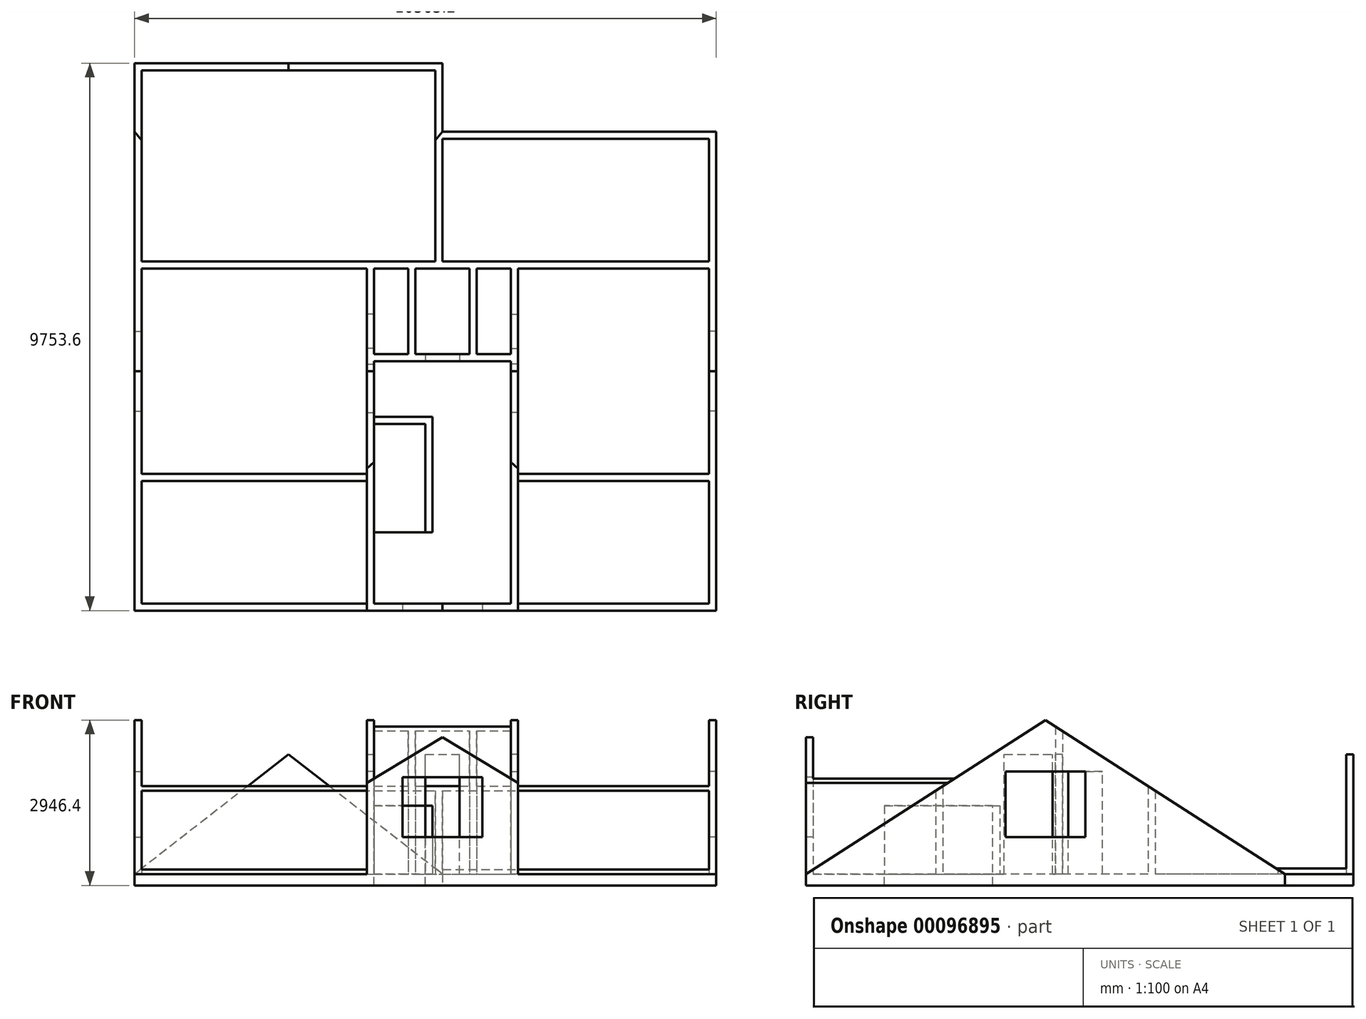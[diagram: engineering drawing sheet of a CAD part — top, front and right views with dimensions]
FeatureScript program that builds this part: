
annotation { "Feature Type Name" : "Feature", "Feature Type Description" : "" }
export const myFeature = defineFeature(function(context is Context, id is Id, definition is map)
    precondition{}
    {
        {
            var Q0;
            Q0=qCreatedBy(makeId("Top.planeOp"),FACE);
            var sketch = newSketch(context, id + "F0", { "sketchPlane" : qUnion([Q0])});
            skLineSegment(sketch, "E0", {"start": v(0, 0) * mm, "end": v(10363.2, 0) * mm});
            skLineSegment(sketch, "E1", {"start": v(10363.2, 0) * mm, "end": v(10363.2, 8534.4) * mm});
            skLineSegment(sketch, "E2", {"start": v(10363.2, 8534.4) * mm, "end": v(5486.4, 8534.4) * mm});
            skLineSegment(sketch, "E3", {"start": v(0, 9753.6) * mm, "end": v(0, 0) * mm});
            skLineSegment(sketch, "E4.bottom", {"start": v(127, 2311.4) * mm, "end": v(4140.2, 2311.4) * mm});
            skLineSegment(sketch, "E4.top", {"start": v(127, 127) * mm, "end": v(4140.2, 127) * mm});
            skLineSegment(sketch, "E4.left", {"start": v(127, 2311.4) * mm, "end": v(127, 127) * mm});
            skLineSegment(sketch, "E4.right", {"start": v(4140.2, 2311.4) * mm, "end": v(4140.2, 127) * mm});
            skLineSegment(sketch, "E5.bottom", {"start": v(4267.2, 127) * mm, "end": v(6705.6, 127) * mm});
            skLineSegment(sketch, "E5.top", {"start": v(4267.2, 4445) * mm, "end": v(6705.6, 4445) * mm});
            skLineSegment(sketch, "E5.left", {"start": v(4267.2, 127) * mm, "end": v(4267.2, 4445) * mm});
            skLineSegment(sketch, "E5.right", {"start": v(6705.6, 127) * mm, "end": v(6705.6, 4445) * mm});
            skLineSegment(sketch, "E6.bottom", {"start": v(6832.6, 2311.4) * mm, "end": v(10236.2, 2311.4) * mm});
            skLineSegment(sketch, "E6.top", {"start": v(6832.6, 127) * mm, "end": v(10236.2, 127) * mm});
            skLineSegment(sketch, "E6.left", {"start": v(6832.6, 2311.4) * mm, "end": v(6832.6, 127) * mm});
            skLineSegment(sketch, "E6.right", {"start": v(10236.2, 2311.4) * mm, "end": v(10236.2, 127) * mm});
            skLineSegment(sketch, "E7.left", {"start": v(127, 9626.6) * mm, "end": v(127, 6223) * mm});
            skLineSegment(sketch, "E8.bottom", {"start": v(5486.4, 8407.4) * mm, "end": v(10236.2, 8407.4) * mm});
            skLineSegment(sketch, "E8.right", {"start": v(10236.2, 8407.4) * mm, "end": v(10236.2, 6223) * mm});
            skLineSegment(sketch, "E9.bottom", {"start": v(4267.2, 6096) * mm, "end": v(4876.8, 6096) * mm});
            skLineSegment(sketch, "E9.top", {"start": v(4267.2, 4572) * mm, "end": v(4876.8, 4572) * mm});
            skLineSegment(sketch, "E9.left", {"start": v(4267.2, 6096) * mm, "end": v(4267.2, 4572) * mm});
            skLineSegment(sketch, "E9.right", {"start": v(4876.8, 6096) * mm, "end": v(4876.8, 4572) * mm});
            skLineSegment(sketch, "E10.bottom", {"start": v(5003.8, 6096) * mm, "end": v(5969, 6096) * mm});
            skLineSegment(sketch, "E10.top", {"start": v(5003.8, 4572) * mm, "end": v(5969, 4572) * mm});
            skLineSegment(sketch, "E10.left", {"start": v(5003.8, 6096) * mm, "end": v(5003.8, 4572) * mm});
            skLineSegment(sketch, "E10.right", {"start": v(5969, 6096) * mm, "end": v(5969, 4572) * mm});
            skLineSegment(sketch, "E11.bottom", {"start": v(6096, 6096) * mm, "end": v(6705.6, 6096) * mm});
            skLineSegment(sketch, "E11.top", {"start": v(6096, 4572) * mm, "end": v(6705.6, 4572) * mm});
            skLineSegment(sketch, "E11.left", {"start": v(6096, 6096) * mm, "end": v(6096, 4572) * mm});
            skLineSegment(sketch, "E11.right", {"start": v(6705.6, 6096) * mm, "end": v(6705.6, 4572) * mm});
            skLineSegment(sketch, "E12.bottom", {"start": v(127, 6096) * mm, "end": v(4140.2, 6096) * mm});
            skLineSegment(sketch, "E12.top", {"start": v(127, 2438.4) * mm, "end": v(4140.2, 2438.4) * mm});
            skLineSegment(sketch, "E12.left", {"start": v(127, 6096) * mm, "end": v(127, 2438.4) * mm});
            skLineSegment(sketch, "E12.right", {"start": v(4140.2, 6096) * mm, "end": v(4140.2, 2438.4) * mm});
            skLineSegment(sketch, "E13.bottom", {"start": v(6832.6, 6096) * mm, "end": v(10236.2, 6096) * mm});
            skLineSegment(sketch, "E13.top", {"start": v(6832.6, 2438.4) * mm, "end": v(10236.2, 2438.4) * mm});
            skLineSegment(sketch, "E13.left", {"start": v(6832.6, 6096) * mm, "end": v(6832.6, 2438.4) * mm});
            skLineSegment(sketch, "E13.right", {"start": v(10236.2, 6096) * mm, "end": v(10236.2, 2438.4) * mm});
            skLineSegment(sketch, "E14", {"start": v(0, 9753.6) * mm, "end": v(5486.4, 9753.6) * mm});
            skLineSegment(sketch, "E15", {"start": v(127, 6223) * mm, "end": v(5359.4, 6223) * mm});
            skLineSegment(sketch, "E16", {"start": v(5486.4, 9753.6) * mm, "end": v(5486.4, 8534.4) * mm});
            skLineSegment(sketch, "E17", {"start": v(127, 9626.6) * mm, "end": v(5359.4, 9626.6) * mm});
            skLineSegment(sketch, "E18", {"start": v(5359.4, 9626.6) * mm, "end": v(5359.4, 6223) * mm});
            skLineSegment(sketch, "E19.trimOffspring", {"start": v(5486.4, 8407.4) * mm, "end": v(5486.4, 6223) * mm});
            skLineSegment(sketch, "E20.trimOffspring", {"start": v(5486.4, 6223) * mm, "end": v(10236.2, 6223) * mm});
            skSolve(sketch);
        }
        {
            var Q0;
            Q0 = qSketchRegion(id + "F0", true);
            extrude(context, id + "F1", {"entities" : qUnion([Q0]), "depth" : 2743.2 * mm});
        }
        {
            var Q0;
            Q0=qCreatedBy(makeId("Top.planeOp"),FACE);
            var sketch = newSketch(context, id + "F2", { "sketchPlane" : qUnion([Q0])});
            skLineSegment(sketch, "E21.bottom", {"start": v(4267.2, 3327.4) * mm, "end": v(5181.6, 3327.4) * mm});
            skLineSegment(sketch, "E21.top", {"start": v(4267.2, 1397) * mm, "end": v(5181.6, 1397) * mm});
            skLineSegment(sketch, "E21.left", {"start": v(4267.2, 3327.4) * mm, "end": v(4267.2, 1397) * mm});
            skLineSegment(sketch, "E21.right", {"start": v(5181.6, 3327.4) * mm, "end": v(5181.6, 1397) * mm});
            skLineSegment(sketch, "E22", {"start": v(0, 0) * mm, "end": v(0, 9753.6) * mm});
            skLineSegment(sketch, "E23", {"start": v(0, 9753.6) * mm, "end": v(5486.4, 9753.6) * mm});
            skLineSegment(sketch, "E24", {"start": v(5486.4, 9753.6) * mm, "end": v(5486.4, 8534.4) * mm});
            skLineSegment(sketch, "E25", {"start": v(5486.4, 8534.4) * mm, "end": v(10363.2, 8534.4) * mm});
            skLineSegment(sketch, "E26", {"start": v(10363.2, 8534.4) * mm, "end": v(10363.2, 0) * mm});
            skLineSegment(sketch, "E27", {"start": v(10363.2, 0) * mm, "end": v(0, 0) * mm});
            skSolve(sketch);
        }
        {
            var Q0;
            Q0 = qSketchRegion(id + "F2", true);
            extrude(context, id + "F3", {"entities" : qUnion([Q0]), "operationType" : NewBodyOperationType.ADD, "oppositeDirection" : true, "depth" : 203.2 * mm});
        }
        {
            var Q0;
            Q0=makeQuery(id+"F1.opExtrude","SWEPT_FACE",FACE,{"disambiguationData":[OSD([sQuery(id+"F0.wireOp",EDGE,"E5.right")])]});
            var sketch = newSketch(context, id + "F4", { "sketchPlane" : qUnion([Q0])});
            skLineSegment(sketch, "E28.bottom", {"start": v(-4394.2, 0) * mm, "end": v(-3530.6, 0) * mm});
            skLineSegment(sketch, "E28.top", {"start": v(-4394.2, 2133.6) * mm, "end": v(-3530.6, 2133.6) * mm});
            skLineSegment(sketch, "E28.left", {"start": v(-4394.2, 0) * mm, "end": v(-4394.2, 2133.6) * mm});
            skLineSegment(sketch, "E28.right", {"start": v(-3530.6, 0) * mm, "end": v(-3530.6, 2133.6) * mm});
            skSolve(sketch);
        }
        {
            var Q0;
            Q0 = qSketchRegion(id + "F4", true);
            extrude(context, id + "F5", {"entities" : qUnion([Q0]), "operationType" : NewBodyOperationType.REMOVE, "endBound" : BoundingType.UP_TO_NEXT, "oppositeDirection" : true, "depth" : 25.4 * mm});
        }
        {
            var Q0;
            Q0=makeQuery(id+"F3.boolean.opBoolean","MERGE",FACE,{"derivedFrom":[makeQuery(id+"F1.opExtrude","SWEPT_FACE",FACE,{"disambiguationData":[OSD([sQuery(id+"F0.wireOp",EDGE,"E5.left")])]}),makeQuery(id+"F3.opExtrude","SWEPT_FACE",FACE,{"disambiguationData":[OSD([sQuery(id+"F2.wireOp",EDGE,"E21.left")])]})]});
            var sketch = newSketch(context, id + "F6", { "sketchPlane" : qUnion([Q0])});
            skLineSegment(sketch, "E29.bottom", {"start": v(3530.6, 0) * mm, "end": v(4394.2, 0) * mm});
            skLineSegment(sketch, "E29.top", {"start": v(3530.6, 2133.6) * mm, "end": v(4394.2, 2133.6) * mm});
            skLineSegment(sketch, "E29.left", {"start": v(3530.6, 0) * mm, "end": v(3530.6, 2133.6) * mm});
            skLineSegment(sketch, "E29.right", {"start": v(4394.2, 0) * mm, "end": v(4394.2, 2133.6) * mm});
            skSolve(sketch);
        }
        {
            var Q0;
            Q0 = qSketchRegion(id + "F6", true);
            extrude(context, id + "F7", {"entities" : qUnion([Q0]), "operationType" : NewBodyOperationType.REMOVE, "endBound" : BoundingType.UP_TO_NEXT, "oppositeDirection" : true, "depth" : 25.4 * mm});
        }
        {
            var Q0;
            Q0=makeQuery(id+"F1.opExtrude","SWEPT_FACE",FACE,{"disambiguationData":[OSD([sQuery(id+"F0.wireOp",EDGE,"E5.top")])]});
            var sketch = newSketch(context, id + "F8", { "sketchPlane" : qUnion([Q0])});
            skLineSegment(sketch, "E30.bottom", {"start": v(5181.6, 0) * mm, "end": v(5791.2, 0) * mm});
            skLineSegment(sketch, "E30.top", {"start": v(5181.6, 2133.6) * mm, "end": v(5791.2, 2133.6) * mm});
            skLineSegment(sketch, "E30.left", {"start": v(5181.6, 0) * mm, "end": v(5181.6, 2133.6) * mm});
            skLineSegment(sketch, "E30.right", {"start": v(5791.2, 0) * mm, "end": v(5791.2, 2133.6) * mm});
            skSolve(sketch);
        }
        {
            var Q0;
            Q0 = qSketchRegion(id + "F8", true);
            extrude(context, id + "F9", {"entities" : qUnion([Q0]), "operationType" : NewBodyOperationType.REMOVE, "endBound" : BoundingType.UP_TO_NEXT, "oppositeDirection" : true, "depth" : 25.4 * mm});
        }
        {
            var Q0;
            Q0=makeQuery(id+"F1.opExtrude","SWEPT_FACE",FACE,{"disambiguationData":[OSD([sQuery(id+"F0.wireOp",EDGE,"E13.right")])]});
            var sketch = newSketch(context, id + "F10", { "sketchPlane" : qUnion([Q0])});
            skLineSegment(sketch, "E31.bottom", {"start": v(-4978.4, 1828.8) * mm, "end": v(-3556, 1828.8) * mm});
            skLineSegment(sketch, "E31.top", {"start": v(-4978.4, 660.4) * mm, "end": v(-3556, 660.4) * mm});
            skLineSegment(sketch, "E31.left", {"start": v(-4978.4, 1828.8) * mm, "end": v(-4978.4, 660.4) * mm});
            skLineSegment(sketch, "E31.right", {"start": v(-3556, 1828.8) * mm, "end": v(-3556, 660.4) * mm});
            skSolve(sketch);
        }
        {
            var Q0;
            Q0 = qSketchRegion(id + "F10", true);
            extrude(context, id + "F11", {"entities" : qUnion([Q0]), "operationType" : NewBodyOperationType.REMOVE, "endBound" : BoundingType.UP_TO_NEXT, "oppositeDirection" : true, "depth" : 25.4 * mm});
        }
        {
            var Q0;
            Q0=makeQuery(id+"F1.opExtrude","SWEPT_FACE",FACE,{"disambiguationData":[OSD([sQuery(id+"F0.wireOp",EDGE,"E13.left")])]});
            var sketch = newSketch(context, id + "F12", { "sketchPlane" : qUnion([Q0])});
            skLineSegment(sketch, "E32.bottom", {"start": v(4673.6, 0) * mm, "end": v(5283.2, 0) * mm});
            skLineSegment(sketch, "E32.top", {"start": v(4673.6, 1828.8) * mm, "end": v(5283.2, 1828.8) * mm});
            skLineSegment(sketch, "E32.left", {"start": v(4673.6, 0) * mm, "end": v(4673.6, 1828.8) * mm});
            skLineSegment(sketch, "E32.right", {"start": v(5283.2, 0) * mm, "end": v(5283.2, 1828.8) * mm});
            skSolve(sketch);
        }
        {
            var Q0;
            Q0 = qSketchRegion(id + "F12", true);
            extrude(context, id + "F13", {"entities" : qUnion([Q0]), "operationType" : NewBodyOperationType.REMOVE, "endBound" : BoundingType.UP_TO_NEXT, "oppositeDirection" : true, "depth" : 25.4 * mm});
        }
        {
            var Q0;
            Q0=makeQuery(id+"F1.opExtrude","SWEPT_FACE",FACE,{"disambiguationData":[OSD([sQuery(id+"F0.wireOp",EDGE,"E12.left")])]});
            var sketch = newSketch(context, id + "F14", { "sketchPlane" : qUnion([Q0])});
            skLineSegment(sketch, "E33.bottom", {"start": v(3556, 1828.8) * mm, "end": v(4978.4, 1828.8) * mm});
            skLineSegment(sketch, "E33.top", {"start": v(3556, 660.4) * mm, "end": v(4978.4, 660.4) * mm});
            skLineSegment(sketch, "E33.left", {"start": v(3556, 1828.8) * mm, "end": v(3556, 660.4) * mm});
            skLineSegment(sketch, "E33.right", {"start": v(4978.4, 1828.8) * mm, "end": v(4978.4, 660.4) * mm});
            skSolve(sketch);
        }
        {
            var Q0;
            Q0 = qSketchRegion(id + "F14", true);
            extrude(context, id + "F15", {"entities" : qUnion([Q0]), "operationType" : NewBodyOperationType.REMOVE, "endBound" : BoundingType.UP_TO_NEXT, "oppositeDirection" : true, "depth" : 25.4 * mm});
        }
        {
            var Q0;
            Q0=makeQuery(id+"F1.opExtrude","SWEPT_FACE",FACE,{"disambiguationData":[OSD([sQuery(id+"F0.wireOp",EDGE,"E12.right")])]});
            var sketch = newSketch(context, id + "F16", { "sketchPlane" : qUnion([Q0])});
            skLineSegment(sketch, "E34.bottom", {"start": v(-5283.2, 0) * mm, "end": v(-4673.6, 0) * mm});
            skLineSegment(sketch, "E34.top", {"start": v(-5283.2, 1828.8) * mm, "end": v(-4673.6, 1828.8) * mm});
            skLineSegment(sketch, "E34.left", {"start": v(-5283.2, 0) * mm, "end": v(-5283.2, 1828.8) * mm});
            skLineSegment(sketch, "E34.right", {"start": v(-4673.6, 0) * mm, "end": v(-4673.6, 1828.8) * mm});
            skSolve(sketch);
        }
        {
            var Q0;
            Q0 = qSketchRegion(id + "F16", true);
            extrude(context, id + "F17", {"entities" : qUnion([Q0]), "operationType" : NewBodyOperationType.REMOVE, "endBound" : BoundingType.UP_TO_NEXT, "oppositeDirection" : true, "depth" : 25.4 * mm});
        }
        {
            var Q0;
            Q0=makeQuery(id+"F3.boolean.opBoolean","MERGE",FACE,{"derivedFrom":[makeQuery(id+"F1.opExtrude","SWEPT_FACE",FACE,{"disambiguationData":[OSD([sQuery(id+"F0.wireOp",EDGE,"E1")])]}),makeQuery(id+"F3.opExtrude","SWEPT_FACE",FACE,{"disambiguationData":[OSD([sQuery(id+"F2.wireOp",EDGE,"O0DFnVWc-X87s-zQva-5IaV-f9uga9J4KueF")])]})]});
            var sketch = newSketch(context, id + "F18", { "sketchPlane" : qUnion([Q0])});
            skLineSegment(sketch, "E35", {"start": v(0, 0) * mm, "end": v(8534.4, 0) * mm, "construction": true});
            skLineSegment(sketch, "E36", {"start": v(4267.2, 0) * mm, "end": v(4267.2, 2743.2) * mm, "construction": true});
            skPoint(sketch, "E36.endSnap0", {"position": v(4267.2, 2743.2) * mm});
            skLineSegment(sketch, "E37", {"start": v(0, 0) * mm, "end": v(4267.2, 2743.2) * mm});
            skLineSegment(sketch, "E38", {"start": v(8534.4, 0) * mm, "end": v(4267.2, 2743.2) * mm});
            skLineSegment(sketch, "E39", {"start": v(0, 0) * mm, "end": v(0, 2743.2) * mm});
            skLineSegment(sketch, "E40", {"start": v(0, 2743.2) * mm, "end": v(8534.4, 2743.2) * mm});
            skLineSegment(sketch, "E41", {"start": v(8534.4, 2743.2) * mm, "end": v(8534.4, 0) * mm});
            skSolve(sketch);
        }
        {
            var Q0;
            Q0 = qSketchRegion(id + "F18", true);
            extrude(context, id + "F19", {"entities" : qUnion([Q0]), "operationType" : NewBodyOperationType.REMOVE, "endBound" : BoundingType.THROUGH_ALL, "oppositeDirection" : true, "depth" : 25.4 * mm});
        }
        {
            var Q0;
            {var subQ0=sQuery(id+"F2.wireOp",EDGE,"E21.bottom");var subQ1=sQuery(id+"F2.wireOp",EDGE,"E21.top");var subQ2=sQuery(id+"F2.wireOp",EDGE,"E21.left");var subQ3=sQuery(id+"F2.wireOp",EDGE,"E21.right");var subQ4=makeQuery(id+"F3.opExtrude","CAP_FACE",FACE,{"disambiguationData":[OSD([subQ0,subQ1,subQ2,subQ3,sQuery(id+"F2.wireOp",EDGE,"E22"),sQuery(id+"F2.wireOp",EDGE,"E23"),sQuery(id+"F2.wireOp",EDGE,"E24"),sQuery(id+"F2.wireOp",EDGE,"E25"),sQuery(id+"F2.wireOp",EDGE,"E26"),sQuery(id+"F2.wireOp",EDGE,"E27")])],"isStart":true});Q0=makeQuery(id+"F17.boolean.opBoolean","MERGE",FACE,{"derivedFrom":[makeQuery(id+"F3.boolean.opBoolean","SPLIT",FACE,{"disambiguationData":[TD([makeQuery(id+"F1.opExtrude","SWEPT_FACE",FACE,{"disambiguationData":[OSD([sQuery(id+"F0.wireOp",EDGE,"E9.bottom")])]})])],"derivedFrom":subQ4}),makeQuery(id+"F13.boolean.opBoolean","MERGE",FACE,{"derivedFrom":[makeQuery(id+"F3.boolean.opBoolean","SPLIT",FACE,{"disambiguationData":[TD([makeQuery(id+"F1.opExtrude","SWEPT_FACE",FACE,{"disambiguationData":[OSD([sQuery(id+"F0.wireOp",EDGE,"E11.bottom")])]})])],"derivedFrom":subQ4}),makeQuery(id+"F9.boolean.opBoolean","MERGE",FACE,{"derivedFrom":[makeQuery(id+"F3.boolean.opBoolean","SPLIT",FACE,{"disambiguationData":[TD([makeQuery(id+"F1.opExtrude","SWEPT_FACE",FACE,{"disambiguationData":[OSD([sQuery(id+"F0.wireOp",EDGE,"E10.bottom")])]})])],"derivedFrom":subQ4}),makeQuery(id+"F7.boolean.opBoolean","MERGE",FACE,{"derivedFrom":[makeQuery(id+"F3.boolean.opBoolean","SPLIT",FACE,{"disambiguationData":[TD([makeQuery(id+"F1.opExtrude","SWEPT_FACE",FACE,{"disambiguationData":[OSD([sQuery(id+"F0.wireOp",EDGE,"E12.bottom")])]})])],"derivedFrom":subQ4}),makeQuery(id+"F5.boolean.opBoolean","MERGE",FACE,{"derivedFrom":[makeQuery(id+"F3.boolean.opBoolean","SPLIT",FACE,{"disambiguationData":[TD([makeQuery(id+"F1.opExtrude","SWEPT_FACE",FACE,{"disambiguationData":[OSD([sQuery(id+"F0.wireOp",EDGE,"E13.bottom")])]})])],"derivedFrom":subQ4}),makeQuery(id+"F3.boolean.opBoolean","SPLIT",FACE,{"disambiguationData":[TD([makeQuery(id+"F1.opExtrude","SWEPT_FACE",FACE,{"disambiguationData":[OSD([sQuery(id+"F0.wireOp",EDGE,"E5.bottom")])]})])],"derivedFrom":subQ4}),makeQuery(id+"F5.opExtrude","SWEPT_FACE",FACE,{"disambiguationData":[OSD([sQuery(id+"F4.wireOp",EDGE,"E28.bottom")])]})]}),makeQuery(id+"F7.opExtrude","SWEPT_FACE",FACE,{"disambiguationData":[OSD([sQuery(id+"F6.wireOp",EDGE,"E29.bottom")])]})]}),makeQuery(id+"F9.opExtrude","SWEPT_FACE",FACE,{"disambiguationData":[OSD([sQuery(id+"F8.wireOp",EDGE,"E30.bottom")])]})]}),makeQuery(id+"F13.opExtrude","SWEPT_FACE",FACE,{"disambiguationData":[OSD([sQuery(id+"F12.wireOp",EDGE,"E32.bottom")])]})]}),makeQuery(id+"F17.opExtrude","SWEPT_FACE",FACE,{"disambiguationData":[OSD([sQuery(id+"F16.wireOp",EDGE,"E34.bottom")])]})]});}
            var sketch = newSketch(context, id + "F20", { "sketchPlane" : qUnion([Q0])});
            skLineSegment(sketch, "E42", {"start": v(4267.2, 3327.4) * mm, "end": v(5181.6, 3327.4) * mm});
            skLineSegment(sketch, "E43", {"start": v(5181.6, 3327.4) * mm, "end": v(5181.6, 1397) * mm});
            skLineSegment(sketch, "E44", {"start": v(5181.6, 1397) * mm, "end": v(5308.6, 1397) * mm});
            skLineSegment(sketch, "E45", {"start": v(5308.6, 1397) * mm, "end": v(5308.6, 3454.4) * mm});
            skLineSegment(sketch, "E46", {"start": v(5308.6, 3454.4) * mm, "end": v(4267.2, 3454.4) * mm});
            skPoint(sketch, "E46.endSnap0", {"position": v(4267.2, 3429) * mm});
            skLineSegment(sketch, "E47", {"start": v(4267.2, 3454.4) * mm, "end": v(4267.2, 3327.4) * mm});
            skSolve(sketch);
        }
        {
            var Q0;
            Q0 = qSketchRegion(id + "F20", true);
            extrude(context, id + "F21", {"entities" : qUnion([Q0]), "operationType" : NewBodyOperationType.ADD, "depth" : 1219.2 * mm});
        }
        {
            var Q0;
            Q0=makeQuery(id+"F3.boolean.opBoolean","MERGE",FACE,{"derivedFrom":[makeQuery(id+"F1.opExtrude","SWEPT_FACE",FACE,{"disambiguationData":[OSD([sQuery(id+"F0.wireOp",EDGE,"E0")])]}),makeQuery(id+"F3.opExtrude","SWEPT_FACE",FACE,{"disambiguationData":[OSD([sQuery(id+"F2.wireOp",EDGE,"E27")])]})]});
            var sketch = newSketch(context, id + "F22", { "sketchPlane" : qUnion([Q0])});
            skLineSegment(sketch, "E48", {"start": v(4140.2, 0) * mm, "end": v(6832.6, 0) * mm});
            skLineSegment(sketch, "E49", {"start": v(5486.4, 0) * mm, "end": v(5486.4, 2438.4) * mm, "construction": true});
            skLineSegment(sketch, "E50", {"start": v(4140.2, 0) * mm, "end": v(4140.2, 1625.6) * mm});
            skLineSegment(sketch, "E51", {"start": v(4140.2, 1625.6) * mm, "end": v(5486.4, 2438.4) * mm});
            skLineSegment(sketch, "E52.MirrorCS", {"start": v(6832.6, 1625.6) * mm, "end": v(5486.4, 2438.4) * mm});
            skLineSegment(sketch, "E53.MirrorCS", {"start": v(6832.6, 0) * mm, "end": v(6832.6, 1625.6) * mm});
            skLineSegment(sketch, "E54.bottom", {"start": v(4775.2, 1727.2) * mm, "end": v(6197.6, 1727.2) * mm});
            skLineSegment(sketch, "E54.top", {"start": v(4775.2, 660.4) * mm, "end": v(6197.6, 660.4) * mm});
            skLineSegment(sketch, "E54.left", {"start": v(4775.2, 1727.2) * mm, "end": v(4775.2, 660.4) * mm});
            skLineSegment(sketch, "E54.right", {"start": v(6197.6, 1727.2) * mm, "end": v(6197.6, 660.4) * mm});
            skPoint(sketch, "E55", {"position": v(5486.4, 660.4) * mm});
            skSolve(sketch);
        }
        {
            var Q0;
            Q0 = qSketchRegion(id + "F22", true);
            extrude(context, id + "F23", {"entities" : qUnion([Q0]), "operationType" : NewBodyOperationType.ADD, "oppositeDirection" : true, "depth" : 127 * mm});
        }
        {
            var Q0;
            Q0=makeQuery(id+"F23.boolean.opBoolean","MERGE",FACE,{"derivedFrom":[makeQuery(id+"F1.opExtrude","SWEPT_FACE",FACE,{"disambiguationData":[OSD([sQuery(id+"F0.wireOp",EDGE,"E5.bottom")])]}),makeQuery(id+"F23.opExtrude","CAP_FACE",FACE,{"disambiguationData":[OSD([sQuery(id+"F22.wireOp",EDGE,"E48"),sQuery(id+"F22.wireOp",EDGE,"E50"),sQuery(id+"F22.wireOp",EDGE,"E51"),sQuery(id+"F22.wireOp",EDGE,"E52.MirrorCS"),sQuery(id+"F22.wireOp",EDGE,"E53.MirrorCS"),sQuery(id+"F22.wireOp",EDGE,"E54.bottom"),sQuery(id+"F22.wireOp",EDGE,"E54.top"),sQuery(id+"F22.wireOp",EDGE,"E54.left"),sQuery(id+"F22.wireOp",EDGE,"E54.right")])],"isStart":false})]});
            var sketch = newSketch(context, id + "F24", { "sketchPlane" : qUnion([Q0])});
            skLineSegment(sketch, "E56", {"start": v(-6705.6, 81.64) * mm, "end": v(-6832.6, 81.64) * mm});
            skLineSegment(sketch, "E57", {"start": v(-6832.6, 81.64) * mm, "end": v(-6832.6, 1625.6) * mm});
            skLineSegment(sketch, "E58", {"start": v(-6832.6, 1625.6) * mm, "end": v(-6705.6, 1702.28) * mm});
            skLineSegment(sketch, "E59", {"start": v(-6705.6, 1702.28) * mm, "end": v(-6705.6, 81.64) * mm});
            skLineSegment(sketch, "E60", {"start": v(-4267.2, 81.64) * mm, "end": v(-4140.2, 81.64) * mm});
            skLineSegment(sketch, "E61", {"start": v(-4140.2, 81.64) * mm, "end": v(-4140.2, 1625.6) * mm});
            skLineSegment(sketch, "E62", {"start": v(-4140.2, 1625.6) * mm, "end": v(-4267.2, 1702.28) * mm});
            skLineSegment(sketch, "E63", {"start": v(-4267.2, 1702.28) * mm, "end": v(-4267.2, 81.64) * mm});
            skSolve(sketch);
        }
        {
            var Q0;
            Q0 = qSketchRegion(id + "F24", true);
            extrude(context, id + "F25", {"entities" : qUnion([Q0]), "operationType" : NewBodyOperationType.ADD, "endBound" : BoundingType.UP_TO_NEXT, "depth" : 25.4 * mm});
        }
        {
            var Q0;
            Q0=makeQuery(id+"F3.boolean.opBoolean","MERGE",FACE,{"derivedFrom":[makeQuery(id+"F1.opExtrude","SWEPT_FACE",FACE,{"disambiguationData":[OSD([sQuery(id+"F0.wireOp",EDGE,"E14")])]}),makeQuery(id+"F3.opExtrude","SWEPT_FACE",FACE,{"disambiguationData":[OSD([sQuery(id+"F2.wireOp",EDGE,"E23")])]})]});
            var sketch = newSketch(context, id + "F26", { "sketchPlane" : qUnion([Q0])});
            skLineSegment(sketch, "E64", {"start": v(-5486.4, 0) * mm, "end": v(0, 0) * mm, "construction": true});
            skLineSegment(sketch, "E65", {"start": v(-2743.2, 0) * mm, "end": v(-2743.2, 2133.6) * mm, "construction": true});
            skLineSegment(sketch, "E66", {"start": v(-2743.2, 2133.6) * mm, "end": v(-5486.4, 0) * mm});
            skLineSegment(sketch, "E67", {"start": v(-5486.4, 2743.2) * mm, "end": v(0, 2743.2) * mm});
            skLineSegment(sketch, "E68", {"start": v(0, 2743.2) * mm, "end": v(0, 0) * mm});
            skLineSegment(sketch, "E69", {"start": v(-2743.2, 2133.6) * mm, "end": v(0, 0) * mm});
            skSolve(sketch);
        }
        {
            var Q0;
            {var subQ1=sQuery(id+"F26.wireOp",EDGE,"E66");Q0=makeQuery(id+"F26.imprint","IMPRINT",FACE,{"disambiguationData":[TD([[makeQuery(id+"F26.imprint","IMPRINT",EDGE,{"derivedFrom":subQ1}),-1.0]])]});}
            extrude(context, id + "F27", {"entities" : qUnion([Q0]), "operationType" : NewBodyOperationType.REMOVE, "oppositeDirection" : true, "depth" : 1219.2 * mm});
        }
        {
            var Q0;
            {var subQ1=sQuery(id+"F0.wireOp",EDGE,"E3");Q0=makeQuery(id+"F19.boolean.opBoolean","COPY",FACE,{"disambiguationData":[TD([makeQuery(id+"F1.opExtrude","SWEPT_FACE",FACE,{"disambiguationData":[OSD([subQ1])]})])],"derivedFrom":makeQuery(id+"F19.opExtrude","SWEPT_FACE",FACE,{"disambiguationData":[OSD([sQuery(id+"F18.wireOp",EDGE,"E41")])]})});}
            var sketch = newSketch(context, id + "F28", { "sketchPlane" : qUnion([Q0])});
            skLineSegment(sketch, "E70", {"start": v(127, 0) * mm, "end": v(127, 98.78) * mm});
            skLineSegment(sketch, "E71", {"start": v(127, 98.78) * mm, "end": v(0, 0) * mm});
            skLineSegment(sketch, "E72", {"start": v(0, 0) * mm, "end": v(127, 0) * mm});
            skSolve(sketch);
        }
        {
            var Q0;
            Q0 = qSketchRegion(id + "F28", true);
            extrude(context, id + "F29", {"entities" : qUnion([Q0]), "operationType" : NewBodyOperationType.ADD, "endBound" : BoundingType.UP_TO_NEXT, "depth" : 25.4 * mm});
        }
        {
            var Q0;
            {var subQ1=sQuery(id+"F0.wireOp",EDGE,"E2");Q0=makeQuery(id+"F19.boolean.opBoolean","COPY",FACE,{"disambiguationData":[TD([makeQuery(id+"F1.opExtrude","SWEPT_FACE",FACE,{"disambiguationData":[OSD([subQ1])]})])],"derivedFrom":makeQuery(id+"F19.opExtrude","SWEPT_FACE",FACE,{"disambiguationData":[OSD([sQuery(id+"F18.wireOp",EDGE,"E41")])]})});}
            var sketch = newSketch(context, id + "F30", { "sketchPlane" : qUnion([Q0])});
            skLineSegment(sketch, "E73", {"start": v(5486.4, 0) * mm, "end": v(5359.4, 98.78) * mm});
            skLineSegment(sketch, "E74", {"start": v(5359.4, 98.78) * mm, "end": v(5359.4, 0) * mm});
            skLineSegment(sketch, "E75", {"start": v(5359.4, 0) * mm, "end": v(5486.4, 0) * mm});
            skSolve(sketch);
        }
        {
            var Q0;
            Q0 = qSketchRegion(id + "F30", true);
            extrude(context, id + "F31", {"entities" : qUnion([Q0]), "operationType" : NewBodyOperationType.ADD, "endBound" : BoundingType.UP_TO_NEXT, "depth" : 25.4 * mm});
        }
    });
